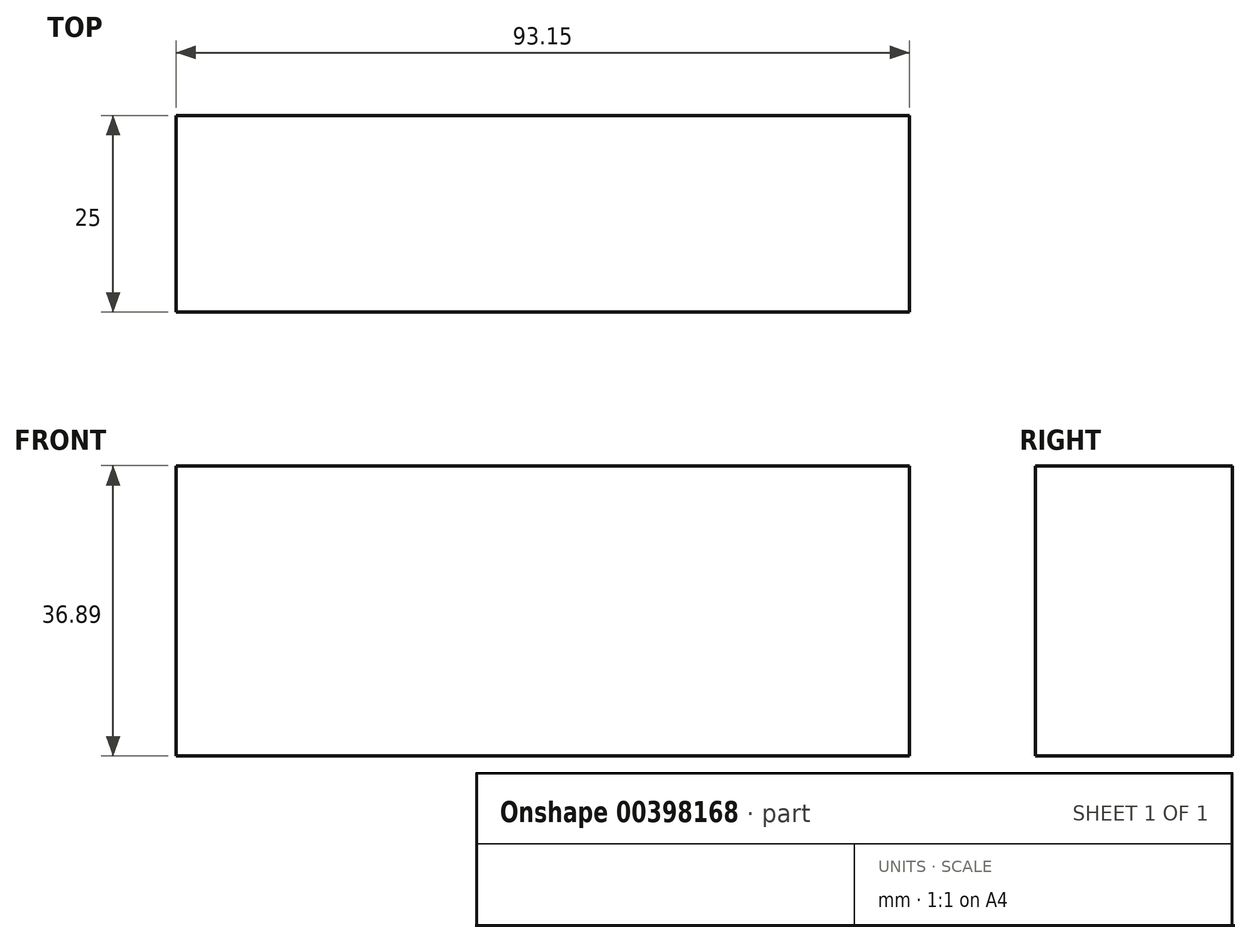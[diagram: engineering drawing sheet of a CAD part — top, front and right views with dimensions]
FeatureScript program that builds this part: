
annotation { "Feature Type Name" : "Feature", "Feature Type Description" : "" }
export const myFeature = defineFeature(function(context is Context, id is Id, definition is map)
    precondition{}
    {
        {
            var Q0;
            Q0=qCreatedBy(makeId("Front.planeOp"),FACE);
            var sketch = newSketch(context, id + "F0", { "sketchPlane" : qUnion([Q0])});
            skLineSegment(sketch, "E0.bottom", {"start": v(-78.55, 28.9) * mm, "end": v(14.6, 28.9) * mm});
            skLineSegment(sketch, "E0.top", {"start": v(-78.55, -7.99) * mm, "end": v(14.6, -7.99) * mm});
            skLineSegment(sketch, "E0.left", {"start": v(-78.55, 28.9) * mm, "end": v(-78.55, -7.99) * mm});
            skLineSegment(sketch, "E0.right", {"start": v(14.6, 28.9) * mm, "end": v(14.6, -7.99) * mm});
            skSolve(sketch);
        }
        {
            var Q0;
            Q0 = qSketchRegion(id + "F0", true);
            extrude(context, id + "F1", {"entities" : qUnion([Q0]), "depth" : 25 * mm});
        }
    });
